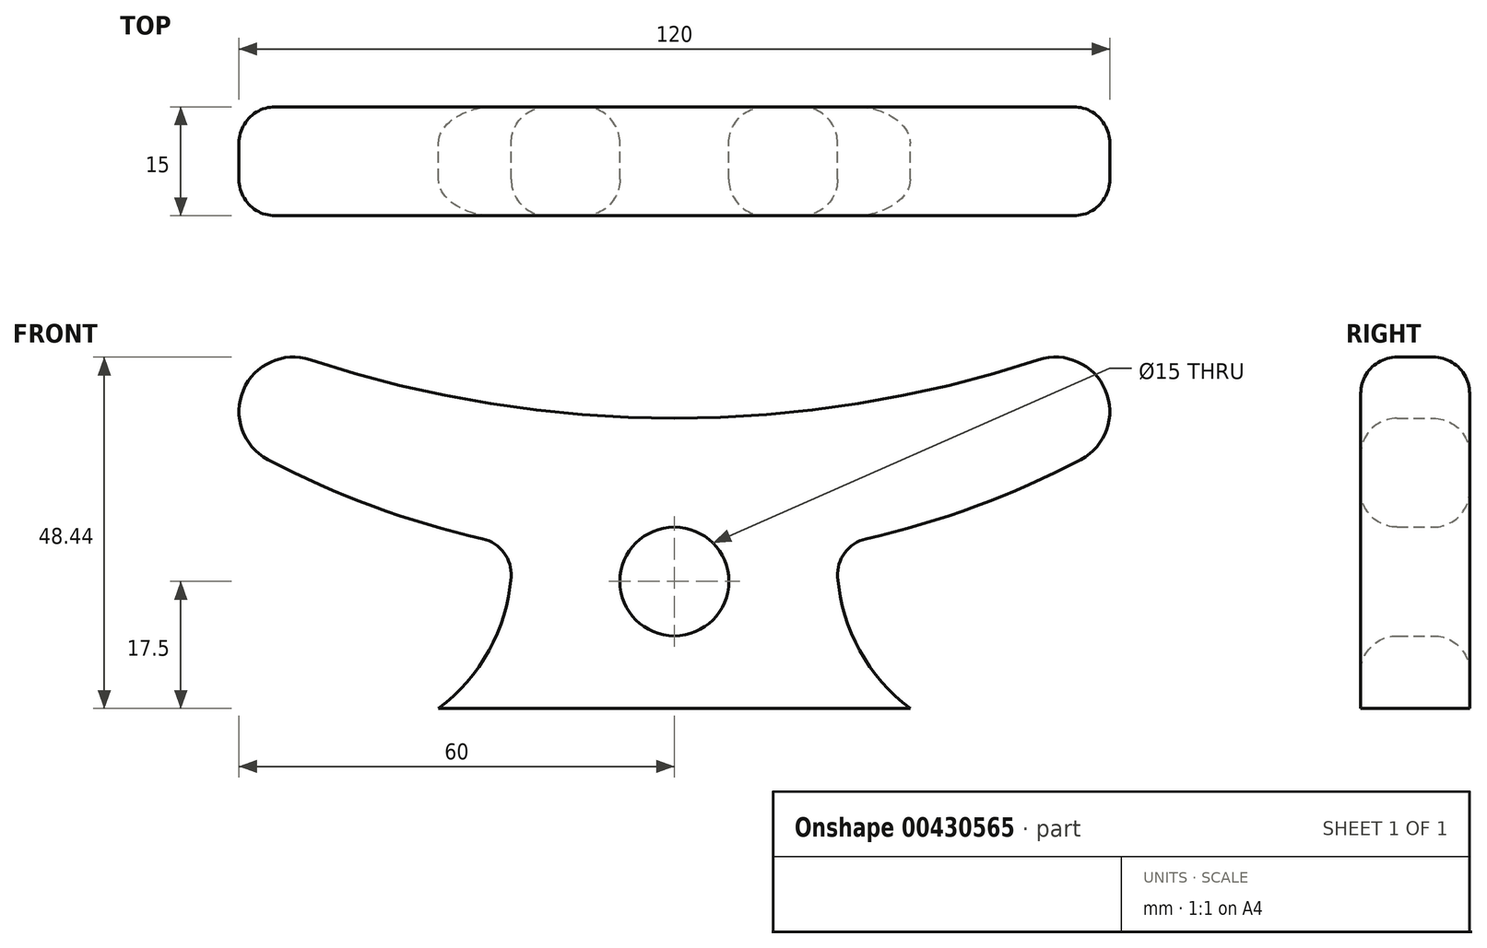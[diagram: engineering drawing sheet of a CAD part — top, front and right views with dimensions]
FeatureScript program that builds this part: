
annotation { "Feature Type Name" : "Feature", "Feature Type Description" : "" }
export const myFeature = defineFeature(function(context is Context, id is Id, definition is map)
    precondition{}
    {
        {
            var Q0;
            Q0=qCreatedBy(makeId("Front.planeOp"),FACE);
            var sketch = newSketch(context, id + "F0", { "sketchPlane" : qUnion([Q0])});
            skArc(sketch, "E0", {"start": v(-50.15, 48.06) * mm, "mid": v(0, 40) * mm, "end": v(50.15, 48.06) * mm});
            skCircle(sketch, "E1", {"center": v(0, 17.5) * mm, "radius": 7.5 * mm});
            skArc(sketch, "E2", {"start": v(22.5, 18.11) * mm, "mid": v(25.54, 7.97) * mm, "end": v(32.5, 0) * mm});
            skArc(sketch, "E3.MirrorC", {"start": v(-22.5, 18.11) * mm, "mid": v(-25.54, 7.97) * mm, "end": v(-32.5, 0) * mm});
            skLineSegment(sketch, "E4", {"start": v(-32.5, 0) * mm, "end": v(32.5, 0) * mm});
            skArc(sketch, "E5", {"start": v(56, 34.3) * mm, "mid": v(59.4, 43.88) * mm, "end": v(50.15, 48.06) * mm});
            skArc(sketch, "E6.MirrorC", {"start": v(-56, 34.3) * mm, "mid": v(-59.4, 43.88) * mm, "end": v(-50.15, 48.06) * mm});
            skArc(sketch, "E7.trimOffspring", {"start": v(-56, 34.3) * mm, "mid": v(-41.56, 27.86) * mm, "end": v(-26.4, 23.38) * mm});
            skArc(sketch, "E8.trimOffspring", {"start": v(26.4, 23.38) * mm, "mid": v(41.56, 27.86) * mm, "end": v(56, 34.3) * mm});
            skPoint(sketch, "E9.visualSharp", {"position": v(22.56, 22.58) * mm});
            skArc(sketch, "E9.filletArc", {"start": v(26.4, 23.38) * mm, "mid": v(23.47, 21.47) * mm, "end": v(22.5, 18.11) * mm});
            skPoint(sketch, "E10.visualSharp", {"position": v(-22.56, 22.58) * mm});
            skArc(sketch, "E10.filletArc", {"start": v(-22.5, 18.11) * mm, "mid": v(-23.47, 21.47) * mm, "end": v(-26.4, 23.38) * mm});
            skSolve(sketch);
        }
        {
            var Q0;
            Q0=makeQuery(id+"F0.imprint","IMPRINT",FACE,{"disambiguationData":[TD([[makeQuery(id+"F0.imprint","IMPRINT",EDGE,{"derivedFrom":sQuery(id+"F0.wireOp",EDGE,"E0")}),-1.0]])]});
            extrude(context, id + "F1", {"entities" : qUnion([Q0]), "depth" : 15 * mm});
        }
        {
            var Q0;
            Q0=makeQuery(id+"F1.opExtrude","CAP_EDGE",EDGE,{"disambiguationData":[OSD([sQuery(id+"F0.wireOp",EDGE,"E0")])],"isStart":false});
            var Q1;
            Q1=makeQuery(id+"F1.opExtrude","CAP_EDGE",EDGE,{"disambiguationData":[OSD([sQuery(id+"F0.wireOp",EDGE,"E0")])],"isStart":true});
            var Q2;
            Q2=makeQuery(id+"F1.opExtrude","CAP_EDGE",EDGE,{"disambiguationData":[OSD([sQuery(id+"F0.wireOp",EDGE,"E1")])],"isStart":true});
            var Q3;
            Q3=makeQuery(id+"F1.opExtrude","CAP_EDGE",EDGE,{"disambiguationData":[OSD([sQuery(id+"F0.wireOp",EDGE,"E1")])],"isStart":false});
            fillet(context, id + "F2", {"entities" : qUnion([Q0, Q1, Q2, Q3]), "radius" : 5 * mm, "tangentPropagation" : true, "allowEdgeOverflow" : false});
        }
    });
